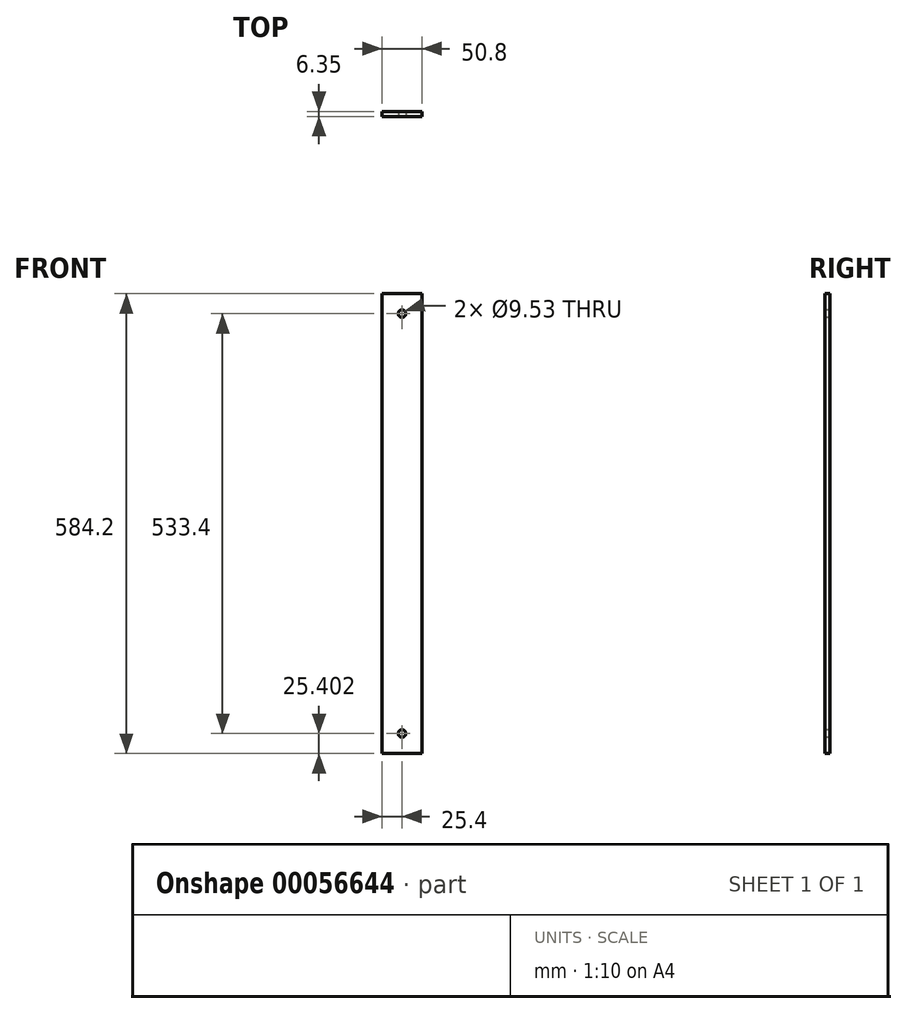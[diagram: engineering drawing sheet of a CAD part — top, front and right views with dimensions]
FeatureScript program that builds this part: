
annotation { "Feature Type Name" : "Feature", "Feature Type Description" : "" }
export const myFeature = defineFeature(function(context is Context, id is Id, definition is map)
    precondition{}
    {
        {
            var Q0;
            Q0=qCreatedBy(makeId("Right.planeOp"),FACE);
            var sketch = newSketch(context, id + "F0", { "sketchPlane" : qUnion([Q0])});
            skLineSegment(sketch, "E0.bottom", {"start": v(-36.23, 337.36) * mm, "end": v(-29.88, 337.36) * mm});
            skLineSegment(sketch, "E0.top", {"start": v(-36.23, -246.84) * mm, "end": v(-29.88, -246.84) * mm});
            skLineSegment(sketch, "E0.left", {"start": v(-36.23, 337.36) * mm, "end": v(-36.23, -246.84) * mm});
            skLineSegment(sketch, "E0.right", {"start": v(-29.88, 337.36) * mm, "end": v(-29.88, -246.84) * mm});
            skSolve(sketch);
        }
        {
            var Q0;
            Q0 = qSketchRegion(id + "F0", true);
            extrude(context, id + "F1", {"entities" : qUnion([Q0]), "endBound" : BoundingType.SYMMETRIC, "depth" : 50.8 * mm});
        }
        {
            var Q0;
            Q0=makeQuery(id+"F1.opExtrude","SWEPT_FACE",FACE,{"disambiguationData":[OSD([sQuery(id+"F0.wireOp",EDGE,"E0.left")])]});
            var sketch = newSketch(context, id + "F2", { "sketchPlane" : qUnion([Q0])});
            skCircle(sketch, "E1", {"center": v(0, 311.96) * mm, "radius": 4.76 * mm});
            skPoint(sketch, "E1.centerSnap0", {"position": v(0, 337.36) * mm});
            skCircle(sketch, "E2", {"center": v(0, -221.44) * mm, "radius": 4.76 * mm});
            skSolve(sketch);
        }
        {
            var Q0;
            Q0 = qSketchRegion(id + "F2", true);
            extrude(context, id + "F3", {"entities" : qUnion([Q0]), "operationType" : NewBodyOperationType.REMOVE, "endBound" : BoundingType.THROUGH_ALL, "oppositeDirection" : true, "depth" : 25.4 * mm});
        }
    });
